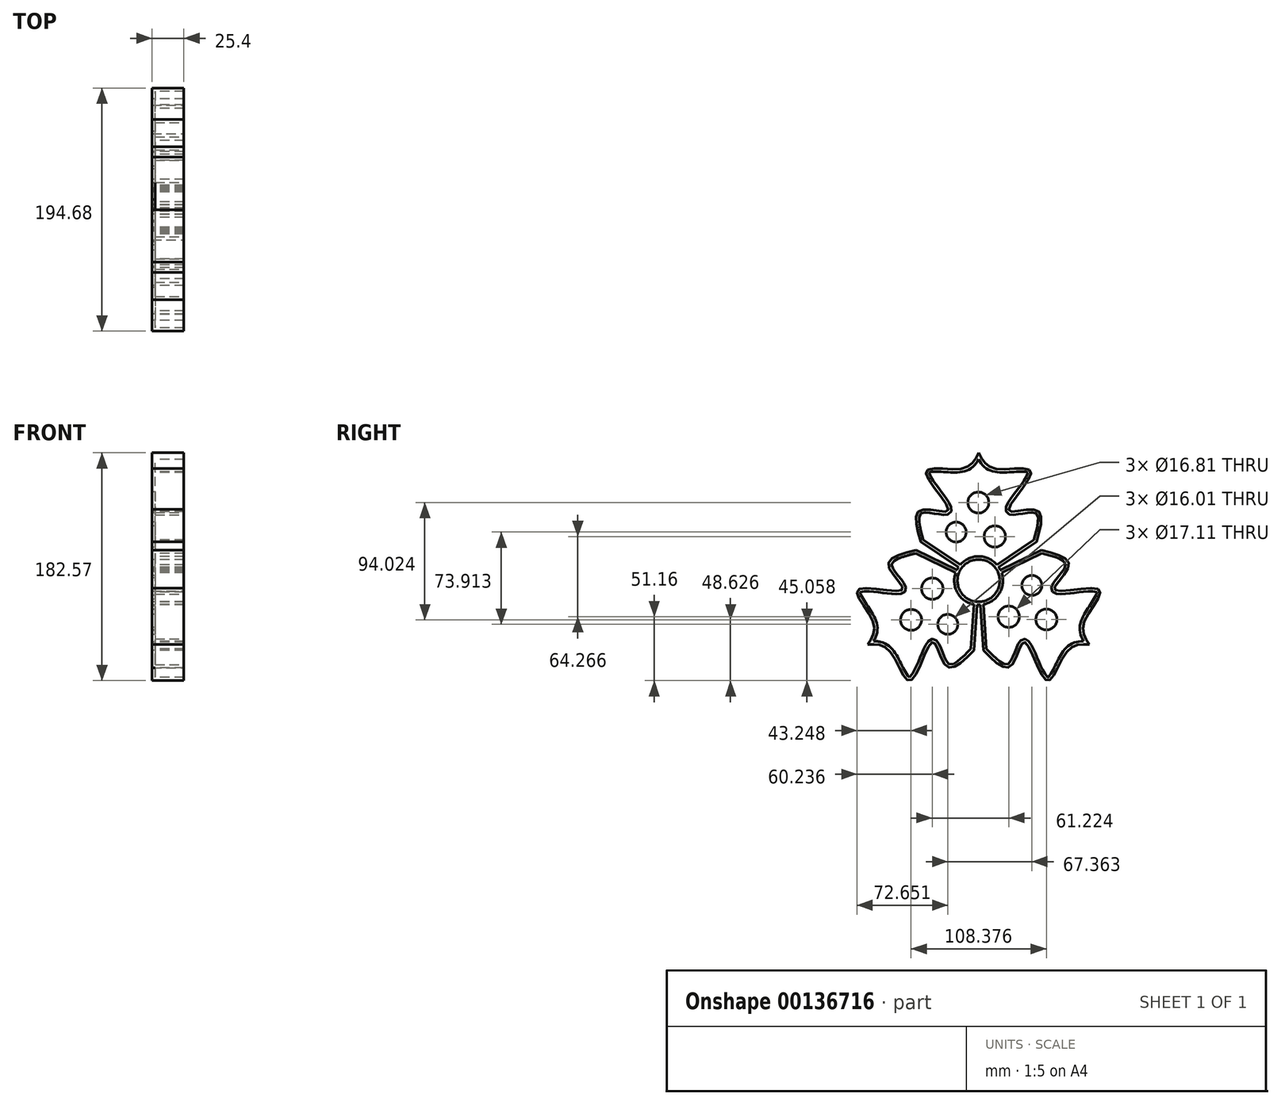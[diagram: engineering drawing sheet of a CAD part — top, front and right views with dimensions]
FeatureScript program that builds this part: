
annotation { "Feature Type Name" : "Feature", "Feature Type Description" : "" }
export const myFeature = defineFeature(function(context is Context, id is Id, definition is map)
    precondition{}
    {
        {
            var Q0;
            Q0=qCreatedBy(makeId("Right.planeOp"),FACE);
            var sketch = newSketch(context, id + "F0", { "sketchPlane" : qUnion([Q0])});
            skFitSpline(sketch, "E0", {"points": [v(46.4, 0) * mm, v(46.4, 25.4) * mm, v(24.3, 25.4) * mm, v(41.98, 55.9) * mm, v(13.7, 58.54) * mm, v(0, 71.36) * mm], "startDerivative": vector(49.69, 173.85) * mm, "endDerivative": vector(-49.98, 100.21) * mm});
            skFitSpline(sketch, "E1.MirrorCS", {"points": [v(-46.4, 0) * mm, v(-46.4, 25.4) * mm, v(-24.3, 25.4) * mm, v(-41.98, 55.9) * mm, v(-13.7, 58.54) * mm, v(0, 71.36) * mm], "startDerivative": vector(-49.69, 173.85) * mm, "endDerivative": vector(49.98, 100.21) * mm});
            skLineSegment(sketch, "E2", {"start": v(-46.4, 0) * mm, "end": v(0, -31.15) * mm});
            skLineSegment(sketch, "E3", {"start": v(0, -31.15) * mm, "end": v(46.4, 0) * mm});
            skSolve(sketch);
        }
        {
            var Q0;
            Q0=makeQuery(id+"F0.imprint","IMPRINT",FACE,{"disambiguationData":[TD([[makeQuery(id+"F0.imprint","IMPRINT",EDGE,{"derivedFrom":sQuery(id+"F0.wireOp",EDGE,"E0")}),1.0]])]});
            extrude(context, id + "F1", {"entities" : qUnion([Q0]), "depth" : 25.4 * mm});
        }
        {
            var Q0;
            Q0=makeQuery(id+"F1.opExtrude","SWEPT_BODY",BODY,{"disambiguationData":[OSD([sQuery(id+"F0.wireOp",EDGE,"E0"),sQuery(id+"F0.wireOp",EDGE,"E1.MirrorCS"),sQuery(id+"F0.wireOp",EDGE,"E2"),sQuery(id+"F0.wireOp",EDGE,"E3")])]});
            var Q1;
            Q1=makeQuery(id+"F1.opExtrude","SWEPT_EDGE",EDGE,{"disambiguationData":[OSD([sQuery(id+"F0.wireOp",EDGE,"E2"),sQuery(id+"F0.wireOp",EDGE,"E3")])]});
            circularPattern(context, id + "F2", {"entities" : qUnion([Q0]), "axis" : qUnion([Q1]), "angle" : 360 * degree, "instanceCount" : 3, "equalSpace" : true});
        }
        {
            var Q0;
            Q0=qCreatedBy(makeId("Right.planeOp"),FACE);
            var sketch = newSketch(context, id + "F3", { "sketchPlane" : qUnion([Q0])});
            skPoint(sketch, "E4.0", {"position": v(0, -31.15) * mm});
            skCircle(sketch, "E5", {"center": v(0, -31.15) * mm, "radius": 16.94 * mm});
            skSolve(sketch);
        }
        {
            var Q0;
            Q0=makeQuery(id+"F3.imprint","IMPRINT",FACE,{"disambiguationData":[TD([[makeQuery(id+"F3.imprint","IMPRINT",EDGE,{"derivedFrom":sQuery(id+"F3.wireOp",EDGE,"E5")}),1.0]])]});
            extrude(context, id + "F4", {"entities" : qUnion([Q0]), "operationType" : NewBodyOperationType.REMOVE, "depth" : 25.4 * mm});
        }
        {
            var Q0;
            Q0=makeQuery(id+"F2.opPattern","COPY",FACE,{"derivedFrom":makeQuery(id+"F1.opExtrude","CAP_FACE",FACE,{"disambiguationData":[OSD([sQuery(id+"F0.wireOp",EDGE,"E0"),sQuery(id+"F0.wireOp",EDGE,"E1.MirrorCS"),sQuery(id+"F0.wireOp",EDGE,"E2"),sQuery(id+"F0.wireOp",EDGE,"E3")])],"isStart":true}),"instanceName":"1"});
            var sketch = newSketch(context, id + "F5", { "sketchPlane" : qUnion([Q0])});
            skCircle(sketch, "E6", {"center": v(0, -31.15) * mm, "radius": 19.4 * mm});
            skArc(sketch, "E7.0", {"start": v(-14.06, -21.7) * mm, "mid": v(0, -14.21) * mm, "end": v(14.06, -21.7) * mm, "construction": true});
            skCircle(sketch, "E8", {"center": v(0, -31.15) * mm, "radius": 16.97 * mm});
            skSolve(sketch);
        }
        {
            var Q0;
            Q0 = qSketchRegion(id + "F5", true);
            extrude(context, id + "F6", {"entities" : qUnion([Q0]), "operationType" : NewBodyOperationType.ADD, "oppositeDirection" : true, "depth" : 25.4 * mm});
        }
        {
            var Q0;
            {var subQ0=makeQuery(id+"F1.opExtrude","CAP_FACE",FACE,{"disambiguationData":[OSD([sQuery(id+"F0.wireOp",EDGE,"E0"),sQuery(id+"F0.wireOp",EDGE,"E1.MirrorCS"),sQuery(id+"F0.wireOp",EDGE,"E2"),sQuery(id+"F0.wireOp",EDGE,"E3")])],"isStart":false});Q0=makeQuery(id+"F6.boolean.opBoolean","MERGE",FACE,{"derivedFrom":[subQ0,makeQuery(id+"F2.opPattern","COPY",FACE,{"derivedFrom":subQ0,"instanceName":"1"}),makeQuery(id+"F2.opPattern","COPY",FACE,{"derivedFrom":subQ0,"instanceName":"2"}),makeQuery(id+"F6.opExtrude","CAP_FACE",FACE,{"disambiguationData":[OSD([sQuery(id+"F5.wireOp",EDGE,"E6"),sQuery(id+"F5.wireOp",EDGE,"E8")])],"isStart":false})]});}
            shell(context, id + "F7", {"entities" : qUnion([Q0]), "thickness" : 2.54 * mm});
        }
        {
            var Q0;
            {var subQ0=makeQuery(id+"F1.opExtrude","CAP_FACE",FACE,{"disambiguationData":[OSD([sQuery(id+"F0.wireOp",EDGE,"E0"),sQuery(id+"F0.wireOp",EDGE,"E1.MirrorCS"),sQuery(id+"F0.wireOp",EDGE,"E2"),sQuery(id+"F0.wireOp",EDGE,"E3")])],"isStart":true});Q0=makeQuery(id+"F6.boolean.opBoolean","MERGE",FACE,{"derivedFrom":[subQ0,makeQuery(id+"F2.opPattern","COPY",FACE,{"derivedFrom":subQ0,"instanceName":"1"}),makeQuery(id+"F2.opPattern","COPY",FACE,{"derivedFrom":subQ0,"instanceName":"2"}),makeQuery(id+"F6.opExtrude","CAP_FACE",FACE,{"disambiguationData":[OSD([sQuery(id+"F5.wireOp",EDGE,"E6"),sQuery(id+"F5.wireOp",EDGE,"E8")])],"isStart":true})]});}
            var sketch = newSketch(context, id + "F8", { "sketchPlane" : qUnion([Q0])});
            skCircle(sketch, "E9", {"center": v(-54.28, -62.25) * mm, "radius": 8.4 * mm});
            skSolve(sketch);
        }
        {
            var Q0;
            Q0 = qSketchRegion(id + "F8", true);
            extrude(context, id + "F9", {"entities" : qUnion([Q0]), "oppositeDirection" : true, "depth" : 25.4 * mm});
        }
        {
            var Q0;
            {var subQ0=makeQuery(id+"F1.opExtrude","CAP_FACE",FACE,{"disambiguationData":[OSD([sQuery(id+"F0.wireOp",EDGE,"E0"),sQuery(id+"F0.wireOp",EDGE,"E1.MirrorCS"),sQuery(id+"F0.wireOp",EDGE,"E2"),sQuery(id+"F0.wireOp",EDGE,"E3")])],"isStart":true});Q0=makeQuery(id+"F6.boolean.opBoolean","MERGE",FACE,{"derivedFrom":[subQ0,makeQuery(id+"F2.opPattern","COPY",FACE,{"derivedFrom":subQ0,"instanceName":"1"}),makeQuery(id+"F2.opPattern","COPY",FACE,{"derivedFrom":subQ0,"instanceName":"2"}),makeQuery(id+"F6.opExtrude","CAP_FACE",FACE,{"disambiguationData":[OSD([sQuery(id+"F5.wireOp",EDGE,"E6"),sQuery(id+"F5.wireOp",EDGE,"E8")])],"isStart":true})]});}
            var sketch = newSketch(context, id + "F10", { "sketchPlane" : qUnion([Q0])});
            skCircle(sketch, "E10", {"center": v(-42.67, -35) * mm, "radius": 8 * mm});
            skCircle(sketch, "E11", {"center": v(-24.12, -60.05) * mm, "radius": 8.55 * mm});
            skSolve(sketch);
        }
        {
            var Q0;
            Q0 = qSketchRegion(id + "F10", true);
            extrude(context, id + "F11", {"entities" : qUnion([Q0]), "oppositeDirection" : true, "depth" : 25.4 * mm});
        }
        {
            var Q0;
            Q0=qCreatedBy(makeId("Front.planeOp"),FACE);
            var sketch = newSketch(context, id + "F12", { "sketchPlane" : qUnion([Q0])});
            skLineSegment(sketch, "E12.0", {"start": v(0, -23.7) * mm, "end": v(0, -48.05) * mm, "construction": true});
            skLineSegment(sketch, "E13.0", {"start": v(0, -21.7) * mm, "end": v(0, -14.21) * mm, "construction": true});
            skLineSegment(sketch, "E14", {"start": v(-28.62, -31.13) * mm, "end": v(32.82, -31.13) * mm});
            skSolve(sketch);
        }
        {
            var Q0;
            Q0=makeQuery(id+"F9.opExtrude","SWEPT_BODY",BODY,{"disambiguationData":[OSD([sQuery(id+"F8.wireOp",EDGE,"E9")])]});
            var Q1;
            Q1=makeQuery(id+"F11.opExtrude","SWEPT_BODY",BODY,{"disambiguationData":[OSD([sQuery(id+"F10.wireOp",EDGE,"E10")])]});
            var Q2;
            Q2=makeQuery(id+"F11.opExtrude","SWEPT_BODY",BODY,{"disambiguationData":[OSD([sQuery(id+"F10.wireOp",EDGE,"E11")])]});
            var Q3;
            Q3=sQuery(id+"F12.wireOp",EDGE,"E14");
            circularPattern(context, id + "F13", {"entities" : qUnion([Q0, Q1, Q2]), "axis" : qUnion([Q3]), "angle" : 360 * degree, "instanceCount" : 3, "equalSpace" : true});
        }
        {
            var Q0;
            Q0=makeQuery(id+"F9.opExtrude","SWEPT_BODY",BODY,{"disambiguationData":[OSD([sQuery(id+"F8.wireOp",EDGE,"E9")])]});
            var Q1;
            Q1=makeQuery(id+"F11.opExtrude","SWEPT_BODY",BODY,{"disambiguationData":[OSD([sQuery(id+"F10.wireOp",EDGE,"E11")])]});
            var Q2;
            Q2=makeQuery(id+"F13.opPattern","COPY",BODY,{"derivedFrom":makeQuery(id+"F11.opExtrude","SWEPT_BODY",BODY,{"disambiguationData":[OSD([sQuery(id+"F10.wireOp",EDGE,"E10")])]}),"instanceName":"1"});
            var Q3;
            Q3=makeQuery(id+"F13.opPattern","COPY",BODY,{"derivedFrom":makeQuery(id+"F9.opExtrude","SWEPT_BODY",BODY,{"disambiguationData":[OSD([sQuery(id+"F8.wireOp",EDGE,"E9")])]}),"instanceName":"2"});
            var Q4;
            Q4=makeQuery(id+"F13.opPattern","COPY",BODY,{"derivedFrom":makeQuery(id+"F11.opExtrude","SWEPT_BODY",BODY,{"disambiguationData":[OSD([sQuery(id+"F10.wireOp",EDGE,"E11")])]}),"instanceName":"2"});
            var Q5;
            Q5=makeQuery(id+"F11.opExtrude","SWEPT_BODY",BODY,{"disambiguationData":[OSD([sQuery(id+"F10.wireOp",EDGE,"E10")])]});
            var Q6;
            Q6=makeQuery(id+"F13.opPattern","COPY",BODY,{"derivedFrom":makeQuery(id+"F11.opExtrude","SWEPT_BODY",BODY,{"disambiguationData":[OSD([sQuery(id+"F10.wireOp",EDGE,"E11")])]}),"instanceName":"1"});
            var Q7;
            Q7=makeQuery(id+"F13.opPattern","COPY",BODY,{"derivedFrom":makeQuery(id+"F9.opExtrude","SWEPT_BODY",BODY,{"disambiguationData":[OSD([sQuery(id+"F8.wireOp",EDGE,"E9")])]}),"instanceName":"1"});
            var Q8;
            Q8=makeQuery(id+"F13.opPattern","COPY",BODY,{"derivedFrom":makeQuery(id+"F11.opExtrude","SWEPT_BODY",BODY,{"disambiguationData":[OSD([sQuery(id+"F10.wireOp",EDGE,"E10")])]}),"instanceName":"2"});
            var Q9;
            Q9=makeQuery(id+"F1.opExtrude","SWEPT_BODY",BODY,{"disambiguationData":[OSD([sQuery(id+"F0.wireOp",EDGE,"E0"),sQuery(id+"F0.wireOp",EDGE,"E1.MirrorCS"),sQuery(id+"F0.wireOp",EDGE,"E2"),sQuery(id+"F0.wireOp",EDGE,"E3")])]});
            booleanBodies(context, id + "F14", {"operationType" : BooleanOperationType.SUBTRACTION, "tools" : qUnion([Q0, Q1, Q2, Q3, Q4, Q5, Q6, Q7, Q8]), "targets" : qUnion([Q9])});
        }
    });
